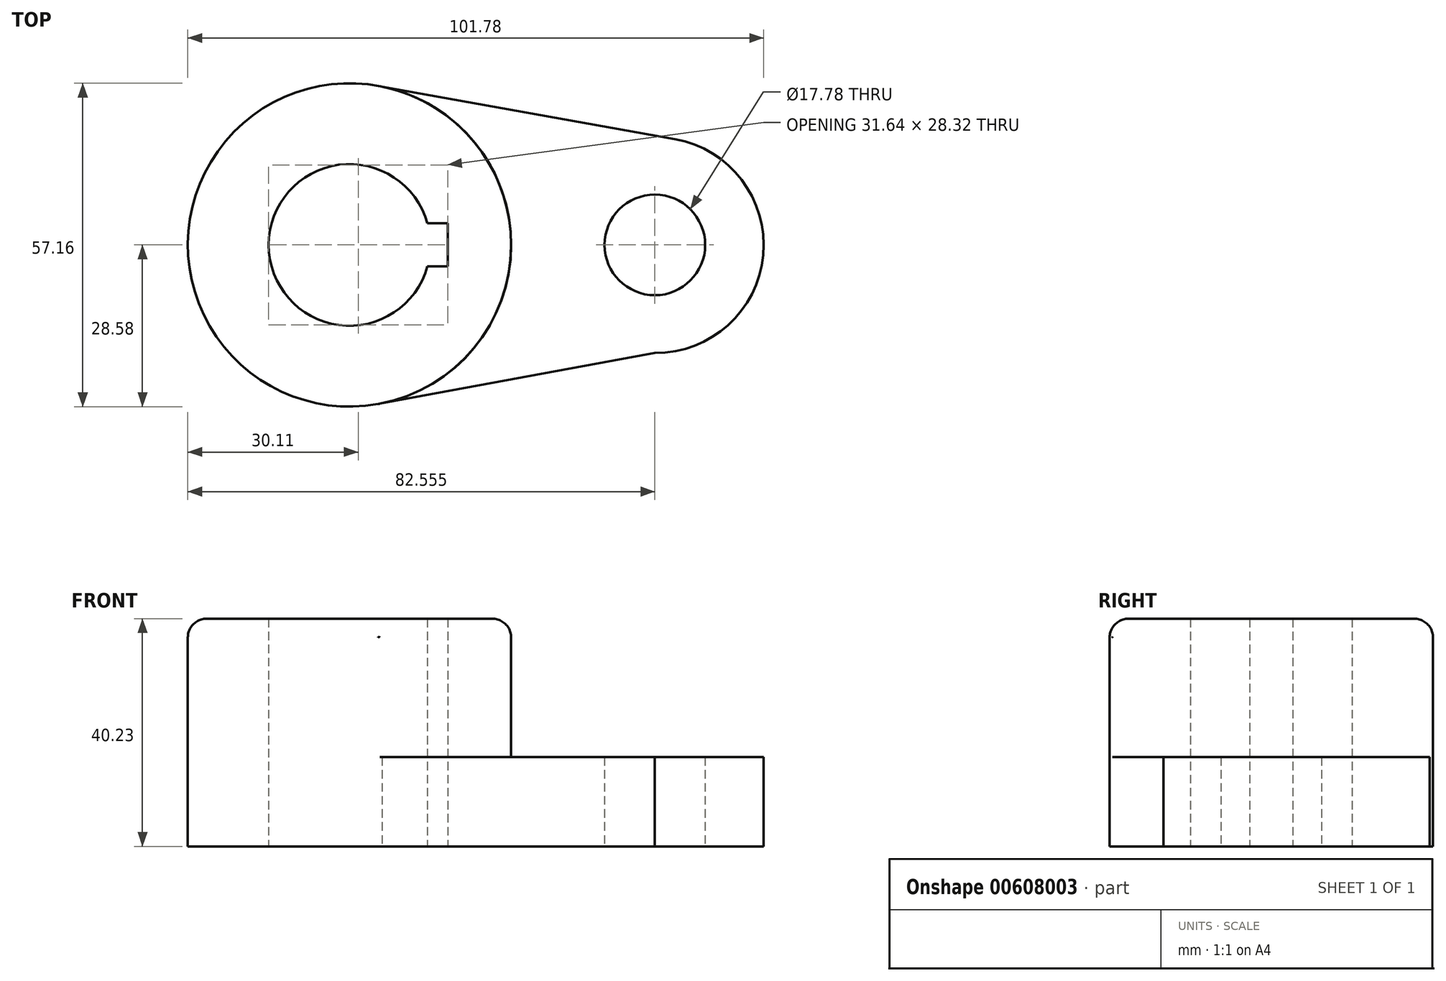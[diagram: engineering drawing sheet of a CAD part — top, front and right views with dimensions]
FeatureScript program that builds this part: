
annotation { "Feature Type Name" : "Feature", "Feature Type Description" : "" }
export const myFeature = defineFeature(function(context is Context, id is Id, definition is map)
    precondition{}
    {
        {
            var Q0;
            Q0=qCreatedBy(makeId("Top.planeOp"),FACE);
            var sketch = newSketch(context, id + "F0", { "sketchPlane" : qUnion([Q0])});
            skCircle(sketch, "E0", {"center": v(0, 0) * mm, "radius": 14.29 * mm});
            skCircle(sketch, "E1", {"center": v(0, 0) * mm, "radius": 28.58 * mm});
            skCircle(sketch, "E2", {"center": v(53.98, 0) * mm, "radius": 8.9 * mm});
            skLineSegment(sketch, "E3", {"start": v(5.72, 28) * mm, "end": v(57.5, 18.73) * mm});
            skLineSegment(sketch, "E4", {"start": v(5.03, -28.13) * mm, "end": v(53.98, -19.08) * mm});
            skArc(sketch, "E5", {"start": v(57.5, 18.73) * mm, "mid": v(73.12, -1.8) * mm, "end": v(53.98, -19.08) * mm});
            skSolve(sketch);
        }
        {
            var Q0;
            Q0=makeQuery(id+"F0.imprint","IMPRINT",FACE,{"disambiguationData":[TD([[makeQuery(id+"F0.imprint","IMPRINT",EDGE,{"derivedFrom":sQuery(id+"F0.wireOp",EDGE,"E0")}),-1.0]])]});
            var Q1;
            Q1=makeQuery(id+"F0.imprint","IMPRINT",FACE,{"disambiguationData":[TD([[makeQuery(id+"F0.imprint","IMPRINT",EDGE,{"derivedFrom":sQuery(id+"F0.wireOp",EDGE,"E2")}),-1.0]])]});
            extrude(context, id + "F1", {"entities" : qUnion([Q0, Q1]), "depth" : 15.77 * mm, "offsetDistance" : 25.4 * mm});
        }
        {
            var Q0;
            Q0=makeQuery(id+"F0.imprint","IMPRINT",FACE,{"disambiguationData":[TD([[makeQuery(id+"F0.imprint","IMPRINT",EDGE,{"derivedFrom":sQuery(id+"F0.wireOp",EDGE,"E0")}),-1.0]])]});
            extrude(context, id + "F2", {"entities" : qUnion([Q0]), "operationType" : NewBodyOperationType.ADD, "depth" : 40.23 * mm, "offsetDistance" : 25.4 * mm});
        }
        {
            var Q0;
            Q0=makeQuery(id+"F0.imprint","IMPRINT",FACE,{"disambiguationData":[TD([[makeQuery(id+"F0.imprint","IMPRINT",EDGE,{"derivedFrom":sQuery(id+"F0.wireOp",EDGE,"E0")}),1.0]])]});
            var sketch = newSketch(context, id + "F3", { "sketchPlane" : qUnion([Q0])});
            skLineSegment(sketch, "E6.bottom", {"start": v(10.9, 3.8) * mm, "end": v(17.35, 3.8) * mm});
            skLineSegment(sketch, "E6.top", {"start": v(10.9, -3.81) * mm, "end": v(17.35, -3.81) * mm});
            skLineSegment(sketch, "E6.left", {"start": v(10.9, 3.81) * mm, "end": v(10.9, -3.81) * mm});
            skLineSegment(sketch, "E6.right", {"start": v(17.35, 3.8) * mm, "end": v(17.35, -3.8) * mm});
            skPoint(sketch, "E6.middle", {"position": v(14.12, 0) * mm});
            skSolve(sketch);
        }
        {
            var Q0;
            {var subQ0=sQuery(id+"F3.wireOp",EDGE,"E6.right");Q0=makeQuery(id+"F3.imprint","IMPRINT",FACE,{"disambiguationData":[TD([[makeQuery(id+"F3.imprint","IMPRINT",EDGE,{"derivedFrom":subQ0}),-1.0]])]});}
            extrude(context, id + "F4", {"entities" : qUnion([Q0]), "operationType" : NewBodyOperationType.REMOVE, "endBound" : BoundingType.THROUGH_ALL, "depth" : 25.4 * mm, "offsetDistance" : 25.4 * mm});
        }
        {
            var Q0;
            Q0=makeQuery(id+"F2.opExtrude","CAP_EDGE",EDGE,{"disambiguationData":[OSD([sQuery(id+"F0.wireOp",EDGE,"E1")])],"isStart":false});
            fillet(context, id + "F5", {"entities" : qUnion([Q0]), "radius" : 3.3 * mm, "tangentPropagation" : true, "allowEdgeOverflow" : false});
        }
    });
